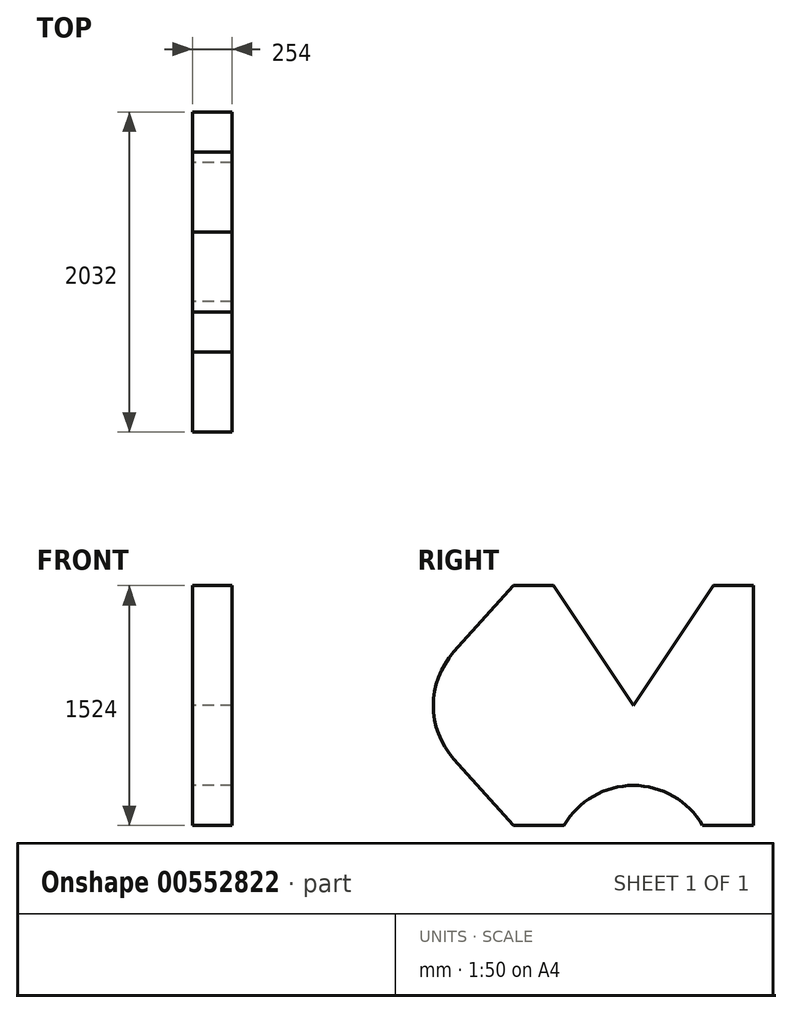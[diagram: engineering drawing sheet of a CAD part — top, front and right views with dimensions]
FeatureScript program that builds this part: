
annotation { "Feature Type Name" : "Feature", "Feature Type Description" : "" }
export const myFeature = defineFeature(function(context is Context, id is Id, definition is map)
    precondition{}
    {
        {
            var Q0;
            Q0=qCreatedBy(makeId("Right.planeOp"),FACE);
            var sketch = newSketch(context, id + "F0", { "sketchPlane" : qUnion([Q0])});
            skLineSegment(sketch, "E0", {"start": v(0, 0) * mm, "end": v(508, 762) * mm});
            skLineSegment(sketch, "E1", {"start": v(508, 762) * mm, "end": v(762, 762) * mm});
            skLineSegment(sketch, "E2", {"start": v(762, 762) * mm, "end": v(762, -762) * mm});
            skLineSegment(sketch, "E3", {"start": v(762, -762) * mm, "end": v(439.94, -762) * mm});
            skLineSegment(sketch, "E4", {"start": v(-439.94, -762) * mm, "end": v(-762, -762) * mm});
            skLineSegment(sketch, "E5", {"start": v(-762, -762) * mm, "end": v(-1140.64, -338.67) * mm});
            skLineSegment(sketch, "E6", {"start": v(0, 0) * mm, "end": v(-508, 762) * mm});
            skLineSegment(sketch, "E7", {"start": v(-508, 762) * mm, "end": v(-762, 762) * mm});
            skLineSegment(sketch, "E8", {"start": v(-762, 762) * mm, "end": v(-1140.64, 338.67) * mm});
            skArc(sketch, "E9", {"start": v(-1140.64, 338.67) * mm, "mid": v(-1270, 0) * mm, "end": v(-1140.64, -338.67) * mm});
            skArc(sketch, "E10", {"start": v(439.94, -762) * mm, "mid": v(0, -508) * mm, "end": v(-439.94, -762) * mm});
            skLineSegment(sketch, "E11", {"start": v(-762, 762) * mm, "end": v(-762, -762) * mm, "construction": true});
            skSolve(sketch);
        }
        {
            var Q0;
            Q0=makeQuery(id+"F0.imprint","IMPRINT",FACE,{"disambiguationData":[TD([[makeQuery(id+"F0.imprint","IMPRINT",EDGE,{"derivedFrom":sQuery(id+"F0.wireOp",EDGE,"E0")}),-1.0]])]});
            extrude(context, id + "F1", {"entities" : qUnion([Q0]), "depth" : 254 * mm, "offsetDistance" : 25.4 * mm});
        }
    });
